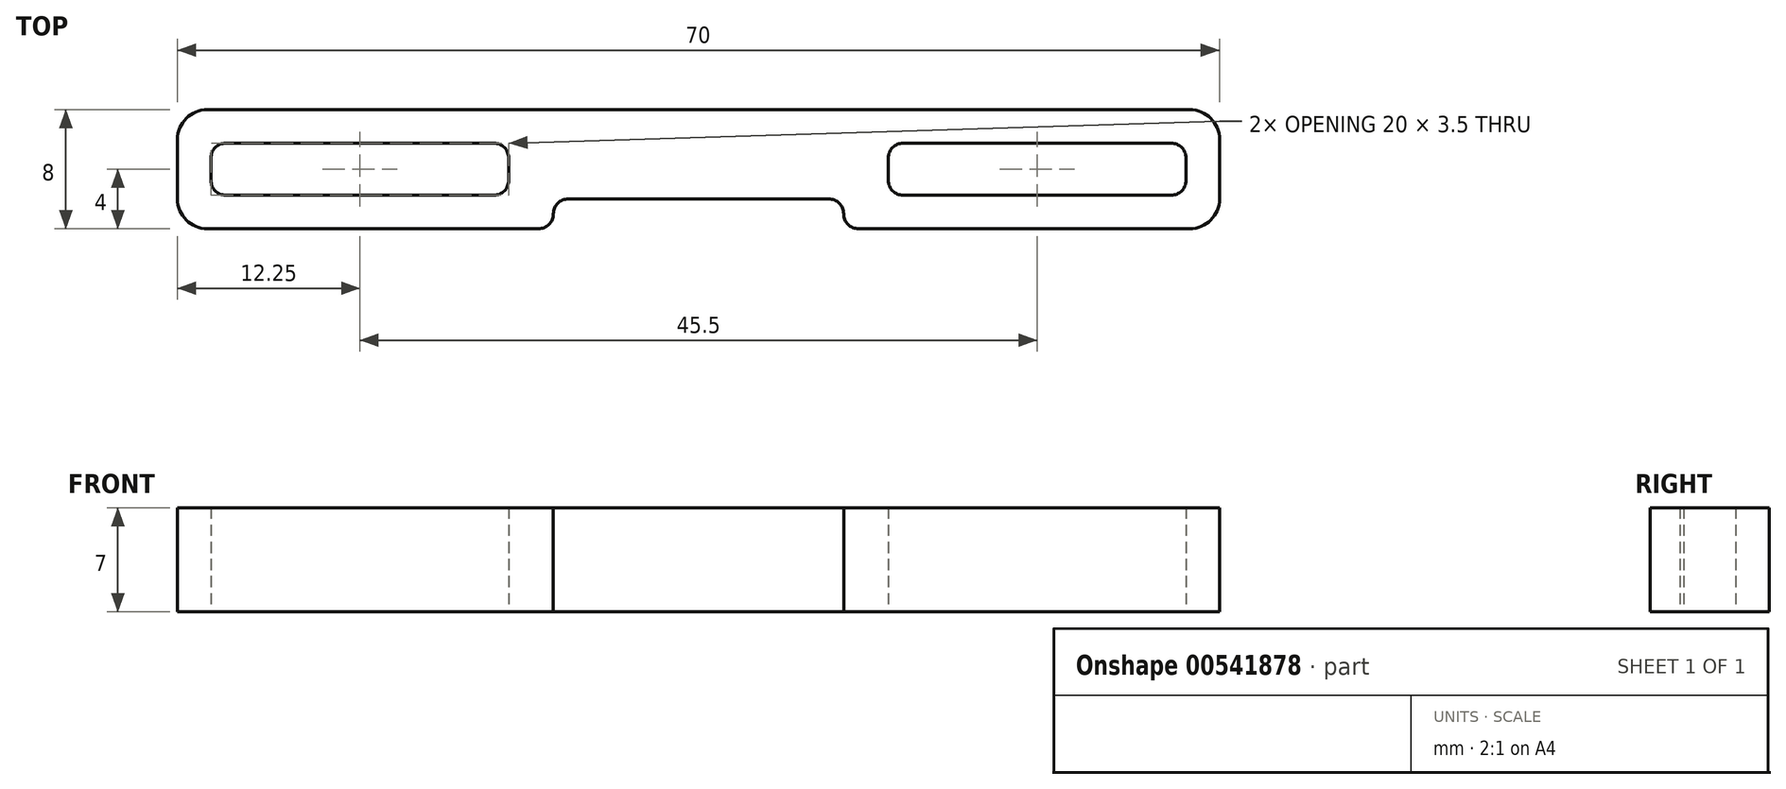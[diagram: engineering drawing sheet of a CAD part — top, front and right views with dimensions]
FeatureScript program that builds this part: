
annotation { "Feature Type Name" : "Feature", "Feature Type Description" : "" }
export const myFeature = defineFeature(function(context is Context, id is Id, definition is map)
    precondition{}
    {
        {
            var Q0;
            Q0=qCreatedBy(makeId("Top.planeOp"),FACE);
            var sketch = newSketch(context, id + "F0", { "sketchPlane" : qUnion([Q0])});
            skLineSegment(sketch, "E0.bottom", {"start": v(35, 4) * mm, "end": v(-35, 4) * mm});
            skLineSegment(sketch, "E0.top", {"start": v(35, -4) * mm, "end": v(9.75, -4) * mm});
            skLineSegment(sketch, "E0.left", {"start": v(35, 4) * mm, "end": v(35, -4) * mm});
            skLineSegment(sketch, "E0.right", {"start": v(-35, 4) * mm, "end": v(-35, -4) * mm});
            skPoint(sketch, "E0.middle", {"position": v(0, 0) * mm});
            skLineSegment(sketch, "E1.0", {"start": v(32.75, 1.75) * mm, "end": v(12.75, 1.75) * mm});
            skLineSegment(sketch, "E2.0", {"start": v(32.75, -1.75) * mm, "end": v(12.75, -1.75) * mm});
            skLineSegment(sketch, "E3.0", {"start": v(-32.75, 1.75) * mm, "end": v(-32.75, -1.75) * mm});
            skLineSegment(sketch, "E4.0", {"start": v(32.75, 1.75) * mm, "end": v(32.75, -1.75) * mm});
            skLineSegment(sketch, "E5.0", {"start": v(-12.75, 1.75) * mm, "end": v(-12.75, -1.75) * mm});
            skLineSegment(sketch, "E6.0", {"start": v(12.75, 1.75) * mm, "end": v(12.75, -1.75) * mm});
            skLineSegment(sketch, "E7.trimOffspring", {"start": v(-12.75, 1.75) * mm, "end": v(-32.75, 1.75) * mm});
            skLineSegment(sketch, "E8.trimOffspring", {"start": v(-12.75, -1.75) * mm, "end": v(-32.75, -1.75) * mm});
            skLineSegment(sketch, "E9.0", {"start": v(9.75, -2) * mm, "end": v(-9.75, -2) * mm});
            skLineSegment(sketch, "E10.0", {"start": v(-9.75, -2) * mm, "end": v(-9.75, -4) * mm});
            skLineSegment(sketch, "E11.0", {"start": v(9.75, -2) * mm, "end": v(9.75, -4) * mm});
            skLineSegment(sketch, "E12.trimOffspring", {"start": v(-9.75, -4) * mm, "end": v(-35, -4) * mm});
            skSolve(sketch);
        }
        {
            var Q0;
            Q0=makeQuery(id+"F0.imprint","IMPRINT",FACE,{"disambiguationData":[TD([[makeQuery(id+"F0.imprint","IMPRINT",EDGE,{"derivedFrom":sQuery(id+"F0.wireOp",EDGE,"E0.bottom")}),1.0]])]});
            extrude(context, id + "F1", {"entities" : qUnion([Q0]), "depth" : 7 * mm, "offsetDistance" : 25 * mm});
        }
        {
            var Q0;
            Q0=makeQuery(id+"F1.opExtrude","SWEPT_EDGE",EDGE,{"disambiguationData":[OSD([sQuery(id+"F0.wireOp",EDGE,"E1.0"),sQuery(id+"F0.wireOp",EDGE,"E4.0")])]});
            var Q1;
            Q1=makeQuery(id+"F1.opExtrude","SWEPT_EDGE",EDGE,{"disambiguationData":[OSD([sQuery(id+"F0.wireOp",EDGE,"E1.0"),sQuery(id+"F0.wireOp",EDGE,"E6.0")])]});
            var Q2;
            Q2=makeQuery(id+"F1.opExtrude","SWEPT_EDGE",EDGE,{"disambiguationData":[OSD([sQuery(id+"F0.wireOp",EDGE,"E2.0"),sQuery(id+"F0.wireOp",EDGE,"E6.0")])]});
            var Q3;
            Q3=makeQuery(id+"F1.opExtrude","SWEPT_EDGE",EDGE,{"disambiguationData":[OSD([sQuery(id+"F0.wireOp",EDGE,"E2.0"),sQuery(id+"F0.wireOp",EDGE,"E4.0")])]});
            var Q4;
            Q4=makeQuery(id+"F1.opExtrude","SWEPT_EDGE",EDGE,{"disambiguationData":[OSD([sQuery(id+"F0.wireOp",EDGE,"E5.0"),sQuery(id+"F0.wireOp",EDGE,"E8.trimOffspring")])]});
            var Q5;
            Q5=makeQuery(id+"F1.opExtrude","SWEPT_EDGE",EDGE,{"disambiguationData":[OSD([sQuery(id+"F0.wireOp",EDGE,"E5.0"),sQuery(id+"F0.wireOp",EDGE,"E7.trimOffspring")])]});
            var Q6;
            Q6=makeQuery(id+"F1.opExtrude","SWEPT_EDGE",EDGE,{"disambiguationData":[OSD([sQuery(id+"F0.wireOp",EDGE,"E3.0"),sQuery(id+"F0.wireOp",EDGE,"E7.trimOffspring")])]});
            var Q7;
            Q7=makeQuery(id+"F1.opExtrude","SWEPT_EDGE",EDGE,{"disambiguationData":[OSD([sQuery(id+"F0.wireOp",EDGE,"E3.0"),sQuery(id+"F0.wireOp",EDGE,"E8.trimOffspring")])]});
            var Q8;
            Q8=makeQuery(id+"FCNzPCkkBA3giEX_1.opFillet","BLEND_EDGE",EDGE,{"blendedFrom":[makeQuery(id+"F1.opExtrude","SWEPT_EDGE",EDGE,{"disambiguationData":[OSD([sQuery(id+"F0.wireOp",EDGE,"E10.0"),sQuery(id+"F0.wireOp",EDGE,"E12.trimOffspring")])]}),makeQuery(id+"F1.opExtrude","SWEPT_FACE",FACE,{"disambiguationData":[OSD([sQuery(id+"F0.wireOp",EDGE,"E9.0")])]})],"blendedInto":[makeQuery(id+"F1.opExtrude","SWEPT_FACE",FACE,{"disambiguationData":[OSD([sQuery(id+"F0.wireOp",EDGE,"E9.0")])]})]});
            var Q9;
            Q9=makeQuery(id+"FCNzPCkkBA3giEX_1.opFillet","BLEND_EDGE",EDGE,{"blendedFrom":[makeQuery(id+"F1.opExtrude","SWEPT_EDGE",EDGE,{"disambiguationData":[OSD([sQuery(id+"F0.wireOp",EDGE,"E0.top"),sQuery(id+"F0.wireOp",EDGE,"E11.0")])]}),makeQuery(id+"F1.opExtrude","SWEPT_FACE",FACE,{"disambiguationData":[OSD([sQuery(id+"F0.wireOp",EDGE,"E9.0")])]})],"blendedInto":[makeQuery(id+"F1.opExtrude","SWEPT_FACE",FACE,{"disambiguationData":[OSD([sQuery(id+"F0.wireOp",EDGE,"E9.0")])]})]});
            fillet(context, id + "F2", {"entities" : qUnion([Q0, Q1, Q2, Q3, Q4, Q5, Q6, Q7, Q8, Q9]), "tangentPropagation" : true, "radius" : 1 * mm, "defaultsChanged" : false, "vertexSettings" : [], "allowEdgeOverflow" : false});
        }
        {
            var Q0;
            Q0=makeQuery(id+"F1.opExtrude","SWEPT_EDGE",EDGE,{"disambiguationData":[OSD([sQuery(id+"F0.wireOp",EDGE,"E0.top"),sQuery(id+"F0.wireOp",EDGE,"E0.left")])]});
            var Q1;
            Q1=makeQuery(id+"F1.opExtrude","SWEPT_EDGE",EDGE,{"disambiguationData":[OSD([sQuery(id+"F0.wireOp",EDGE,"E0.bottom"),sQuery(id+"F0.wireOp",EDGE,"E0.left")])]});
            var Q2;
            Q2=makeQuery(id+"F1.opExtrude","SWEPT_EDGE",EDGE,{"disambiguationData":[OSD([sQuery(id+"F0.wireOp",EDGE,"E0.right"),sQuery(id+"F0.wireOp",EDGE,"E12.trimOffspring")])]});
            var Q3;
            Q3=makeQuery(id+"F1.opExtrude","SWEPT_EDGE",EDGE,{"disambiguationData":[OSD([sQuery(id+"F0.wireOp",EDGE,"E0.bottom"),sQuery(id+"F0.wireOp",EDGE,"E0.right")])]});
            fillet(context, id + "F3", {"entities" : qUnion([Q0, Q1, Q2, Q3]), "tangentPropagation" : true, "radius" : 2 * mm, "defaultsChanged" : false, "vertexSettings" : [], "allowEdgeOverflow" : false});
        }
        {
            var Q0;
            Q0=makeQuery(id+"F1.opExtrude","SWEPT_EDGE",EDGE,{"disambiguationData":[OSD([sQuery(id+"F0.wireOp",EDGE,"E9.0"),sQuery(id+"F0.wireOp",EDGE,"E10.0")])]});
            var Q1;
            Q1=makeQuery(id+"F1.opExtrude","SWEPT_EDGE",EDGE,{"disambiguationData":[OSD([sQuery(id+"F0.wireOp",EDGE,"E10.0"),sQuery(id+"F0.wireOp",EDGE,"E12.trimOffspring")])]});
            var Q2;
            Q2=makeQuery(id+"F1.opExtrude","SWEPT_EDGE",EDGE,{"disambiguationData":[OSD([sQuery(id+"F0.wireOp",EDGE,"E9.0"),sQuery(id+"F0.wireOp",EDGE,"E11.0")])]});
            var Q3;
            Q3=makeQuery(id+"F1.opExtrude","SWEPT_EDGE",EDGE,{"disambiguationData":[OSD([sQuery(id+"F0.wireOp",EDGE,"E0.top"),sQuery(id+"F0.wireOp",EDGE,"E11.0")])]});
            fillet(context, id + "F4", {"entities" : qUnion([Q0, Q1, Q2, Q3]), "tangentPropagation" : true, "radius" : 1 * mm, "defaultsChanged" : false, "vertexSettings" : [], "allowEdgeOverflow" : false});
        }
    });
